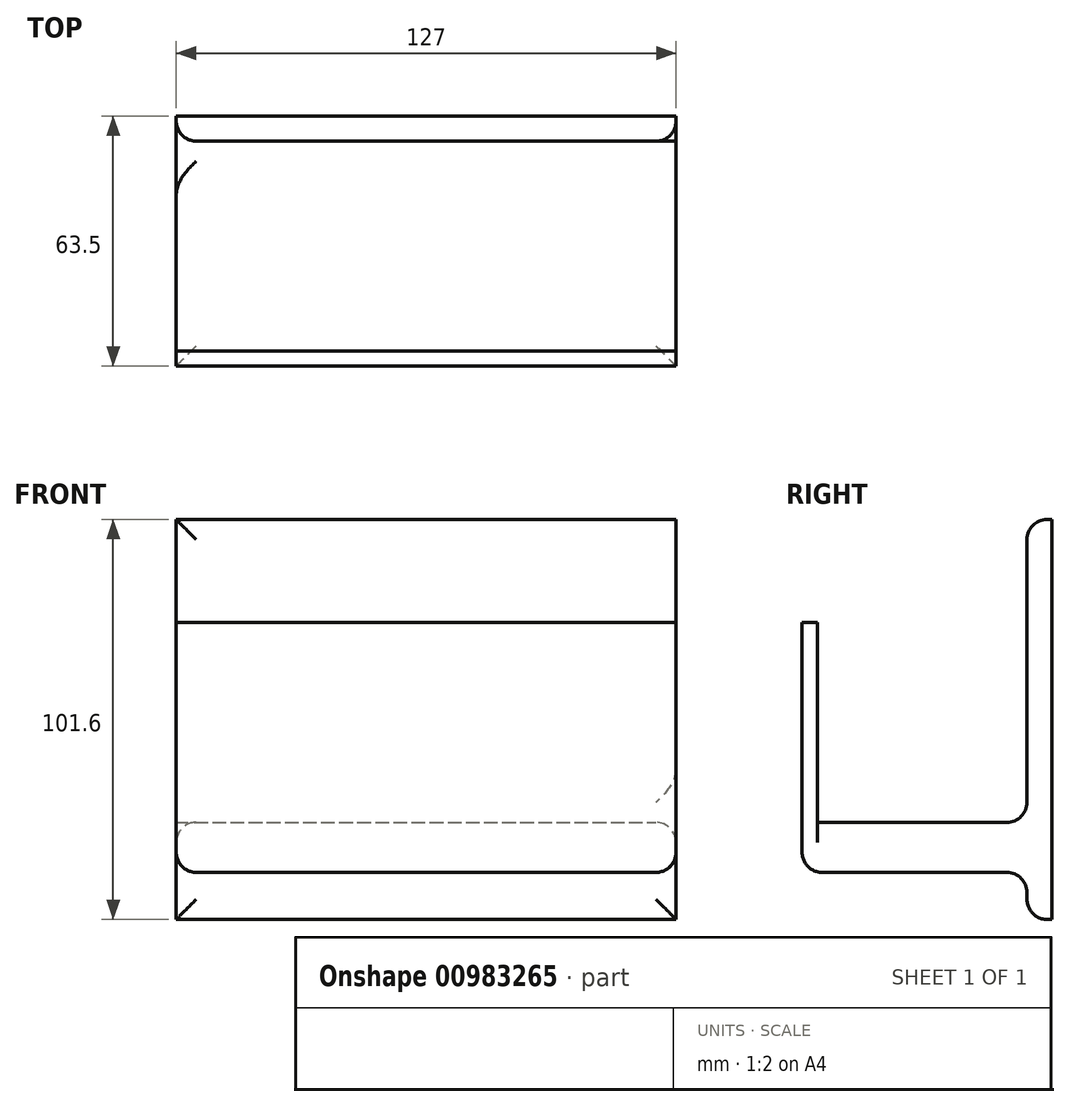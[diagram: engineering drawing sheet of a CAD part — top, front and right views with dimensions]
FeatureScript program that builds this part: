
annotation { "Feature Type Name" : "Feature", "Feature Type Description" : "" }
export const myFeature = defineFeature(function(context is Context, id is Id, definition is map)
    precondition{}
    {
        {
            var Q0;
            Q0=qCreatedBy(makeId("Front.planeOp"),FACE);
            var sketch = newSketch(context, id + "F0", { "sketchPlane" : qUnion([Q0])});
            skLineSegment(sketch, "E0.bottom", {"start": v(-55.94, -1.51) * mm, "end": v(71.06, -1.51) * mm});
            skLineSegment(sketch, "E0.top", {"start": v(-55.94, -14.21) * mm, "end": v(71.06, -14.21) * mm});
            skLineSegment(sketch, "E0.left", {"start": v(-55.94, -1.51) * mm, "end": v(-55.94, -14.21) * mm});
            skLineSegment(sketch, "E0.right", {"start": v(71.06, -1.51) * mm, "end": v(71.06, -14.21) * mm});
            skPoint(sketch, "E1.firstSnap0", {"position": v(-55.94, -7.86) * mm});
            skLineSegment(sketch, "E1.bottom", {"start": v(-55.94, 75.44) * mm, "end": v(71.06, 75.44) * mm});
            skLineSegment(sketch, "E1.top", {"start": v(-55.94, -26.16) * mm, "end": v(71.06, -26.16) * mm});
            skLineSegment(sketch, "E1.left", {"start": v(-55.94, 75.44) * mm, "end": v(-55.94, -26.16) * mm});
            skLineSegment(sketch, "E1.right", {"start": v(71.06, 75.44) * mm, "end": v(71.06, -26.16) * mm});
            skSolve(sketch);
        }
        {
            var Q0;
            Q0=makeQuery(id+"F0.imprint","IMPRINT",FACE,{"disambiguationData":[TD([[makeQuery(id+"F0.imprint","IMPRINT",EDGE,{"derivedFrom":sQuery(id+"F0.wireOp",EDGE,"E0.bottom")}),-1.0]])]});
            extrude(context, id + "F1", {"entities" : qUnion([Q0]), "depth" : 63.5 * mm, "offsetDistance" : 25.4 * mm});
        }
        {
            var Q0;
            {var subQ0=sQuery(id+"F0.wireOp",EDGE,"E0.bottom");var subQ1=makeQuery(id+"F0.imprint","IMPRINT",EDGE,{"derivedFrom":subQ0});var subQ2=sQuery(id+"F0.wireOp",EDGE,"E0.top");var subQ3=makeQuery(id+"F0.imprint","IMPRINT",EDGE,{"derivedFrom":subQ2});Q0=qUnion([makeQuery(id+"F0.imprint","IMPRINT",FACE,{"disambiguationData":[TD([[subQ1,1.0]])]}),makeQuery(id+"F0.imprint","IMPRINT",FACE,{"disambiguationData":[TD([[subQ3,-1.0]])]}),makeQuery(id+"F0.imprint","IMPRINT",FACE,{"disambiguationData":[TD([[subQ1,-1.0]])]})]);}
            extrude(context, id + "F2", {"entities" : qUnion([Q0]), "operationType" : NewBodyOperationType.ADD, "depth" : 6.35 * mm, "offsetDistance" : 25.4 * mm});
        }
        {
            var Q0;
            Q0=makeQuery(id+"F1.opExtrude","SWEPT_FACE",FACE,{"disambiguationData":[OSD([sQuery(id+"F0.wireOp",EDGE,"E0.bottom")])]});
            var sketch = newSketch(context, id + "F3", { "sketchPlane" : qUnion([Q0])});
            skLineSegment(sketch, "E2.bottom", {"start": v(-55.94, -59.65) * mm, "end": v(71.06, -59.65) * mm});
            skLineSegment(sketch, "E2.top", {"start": v(-55.94, -63.5) * mm, "end": v(71.06, -63.5) * mm});
            skLineSegment(sketch, "E2.left", {"start": v(-55.94, -59.65) * mm, "end": v(-55.94, -63.5) * mm});
            skLineSegment(sketch, "E2.right", {"start": v(71.06, -59.65) * mm, "end": v(71.06, -63.5) * mm});
            skSolve(sketch);
        }
        {
            var Q0;
            Q0 = qSketchRegion(id + "F3", true);
            extrude(context, id + "F4", {"entities" : qUnion([Q0]), "operationType" : NewBodyOperationType.ADD, "depth" : 50.8 * mm, "offsetDistance" : 25.4 * mm});
        }
        {
            var Q0;
            Q0=makeQuery(id+"F1.opExtrude","CAP_EDGE",EDGE,{"disambiguationData":[OSD([sQuery(id+"F0.wireOp",EDGE,"E0.top")])],"isStart":false});
            var Q1;
            Q1=makeQuery(id+"F1.opExtrude","SWEPT_EDGE",EDGE,{"disambiguationData":[OSD([sQuery(id+"F0.wireOp",EDGE,"E0.top"),sQuery(id+"F0.wireOp",EDGE,"E0.right"),sQuery(id+"F0.wireOp",EDGE,"E1.right")])]});
            var Q2;
            Q2=makeQuery(id+"F2.opExtrude","CAP_EDGE",EDGE,{"disambiguationData":[OSD([sQuery(id+"F0.wireOp",EDGE,"E1.top")])],"isStart":false});
            var Q3;
            {var subQ0=sQuery(id+"F0.wireOp",EDGE,"E1.left");var subQ2=sQuery(id+"F0.wireOp",EDGE,"E0.left");Q3=makeQuery(id+"F2.boolean.opBoolean","SPLIT",EDGE,{"disambiguationData":[TD([makeQuery(id+"F1.opExtrude","SWEPT_FACE",FACE,{"disambiguationData":[OSD([sQuery(id+"F0.wireOp",EDGE,"E0.top")])]})])],"derivedFrom":makeQuery(id+"F2.opExtrude","CAP_EDGE",EDGE,{"disambiguationData":[OSD([subQ2,subQ0])],"isStart":false})});}
            var Q4;
            Q4=makeQuery(id+"F1.opExtrude","SWEPT_EDGE",EDGE,{"disambiguationData":[OSD([sQuery(id+"F0.wireOp",EDGE,"E0.top"),sQuery(id+"F0.wireOp",EDGE,"E0.left"),sQuery(id+"F0.wireOp",EDGE,"E1.left")])]});
            var Q5;
            {var subQ0=sQuery(id+"F0.wireOp",EDGE,"E1.right");var subQ1=sQuery(id+"F0.wireOp",EDGE,"E0.right");Q5=makeQuery(id+"F2.boolean.opBoolean","SPLIT",EDGE,{"disambiguationData":[TD([makeQuery(id+"F1.opExtrude","SWEPT_FACE",FACE,{"disambiguationData":[OSD([sQuery(id+"F0.wireOp",EDGE,"E0.top")])]})])],"derivedFrom":makeQuery(id+"F2.opExtrude","CAP_EDGE",EDGE,{"disambiguationData":[OSD([subQ1,subQ0])],"isStart":false})});}
            var Q6;
            Q6=makeQuery(id+"F2.boolean.opBoolean","INTERSECT",EDGE,{"derivedFrom":[makeQuery(id+"F1.opExtrude","SWEPT_FACE",FACE,{"disambiguationData":[OSD([sQuery(id+"F0.wireOp",EDGE,"E0.top")])]}),makeQuery(id+"F2.opExtrude","CAP_FACE",FACE,{"disambiguationData":[OSD([sQuery(id+"F0.wireOp",EDGE,"E0.left"),sQuery(id+"F0.wireOp",EDGE,"E0.right"),sQuery(id+"F0.wireOp",EDGE,"E1.bottom"),sQuery(id+"F0.wireOp",EDGE,"E1.top"),sQuery(id+"F0.wireOp",EDGE,"E1.left"),sQuery(id+"F0.wireOp",EDGE,"E1.right")])],"isStart":false})]});
            var Q7;
            {var subQ0=sQuery(id+"F0.wireOp",EDGE,"E1.left");var subQ1=sQuery(id+"F0.wireOp",EDGE,"E0.left");Q7=makeQuery(id+"F2.boolean.opBoolean","SPLIT",EDGE,{"disambiguationData":[TD([makeQuery(id+"F1.opExtrude","SWEPT_FACE",FACE,{"disambiguationData":[OSD([sQuery(id+"F0.wireOp",EDGE,"E0.bottom")])]})])],"derivedFrom":makeQuery(id+"F2.opExtrude","CAP_EDGE",EDGE,{"disambiguationData":[OSD([subQ1,subQ0])],"isStart":false})});}
            var Q8;
            Q8=makeQuery(id+"F2.boolean.opBoolean","INTERSECT",EDGE,{"derivedFrom":[makeQuery(id+"F1.opExtrude","SWEPT_FACE",FACE,{"disambiguationData":[OSD([sQuery(id+"F0.wireOp",EDGE,"E0.bottom")])]}),makeQuery(id+"F2.opExtrude","CAP_FACE",FACE,{"disambiguationData":[OSD([sQuery(id+"F0.wireOp",EDGE,"E0.left"),sQuery(id+"F0.wireOp",EDGE,"E0.right"),sQuery(id+"F0.wireOp",EDGE,"E1.bottom"),sQuery(id+"F0.wireOp",EDGE,"E1.top"),sQuery(id+"F0.wireOp",EDGE,"E1.left"),sQuery(id+"F0.wireOp",EDGE,"E1.right")])],"isStart":false})]});
            var Q9;
            Q9=makeQuery(id+"F2.opExtrude","CAP_EDGE",EDGE,{"disambiguationData":[OSD([sQuery(id+"F0.wireOp",EDGE,"E1.bottom")])],"isStart":false});
            var Q10;
            Q10=makeQuery(id+"F1.opExtrude","SWEPT_EDGE",EDGE,{"disambiguationData":[OSD([sQuery(id+"F0.wireOp",EDGE,"E0.bottom"),sQuery(id+"F0.wireOp",EDGE,"E0.right"),sQuery(id+"F0.wireOp",EDGE,"E1.right")])]});
            fillet(context, id + "F5", {"entities" : qUnion([Q0, Q1, Q2, Q3, Q4, Q5, Q6, Q7, Q8, Q9, Q10]), "tangentPropagation" : true, "radius" : 5.08 * mm, "defaultsChanged" : false, "vertexSettings" : [], "allowEdgeOverflow" : false});
        }
    });
